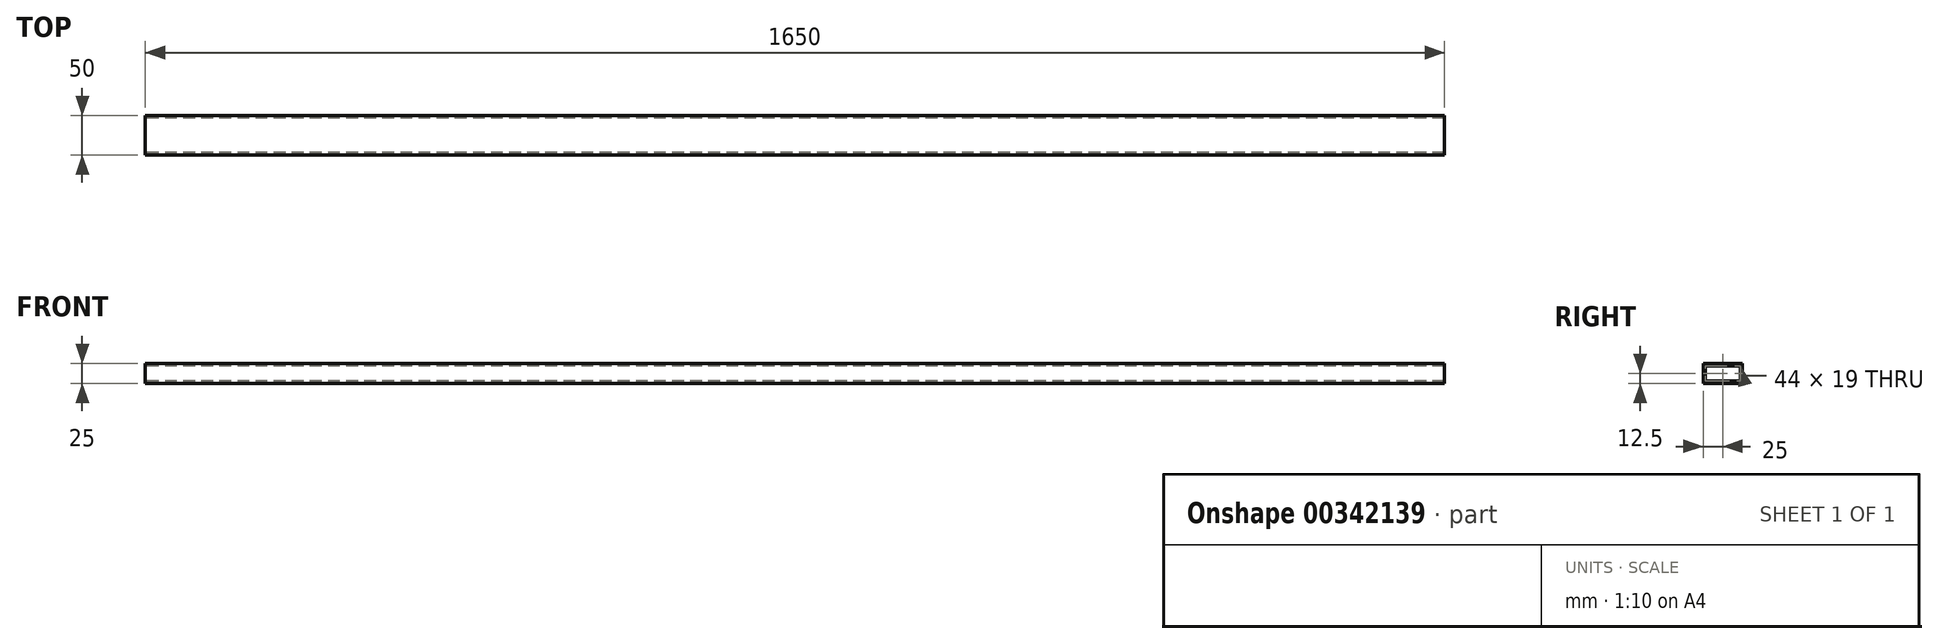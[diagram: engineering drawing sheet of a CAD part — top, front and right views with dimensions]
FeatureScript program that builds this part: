
annotation { "Feature Type Name" : "Feature", "Feature Type Description" : "" }
export const myFeature = defineFeature(function(context is Context, id is Id, definition is map)
    precondition{}
    {
        {
            var Q0;
            Q0=qCreatedBy(makeId("Right.planeOp"),FACE);
            var sketch = newSketch(context, id + "F0", { "sketchPlane" : qUnion([Q0])});
            skLineSegment(sketch, "E0.bottom", {"start": v(-25, 12.5) * mm, "end": v(25, 12.5) * mm});
            skLineSegment(sketch, "E0.top", {"start": v(-25, -12.5) * mm, "end": v(25, -12.5) * mm});
            skLineSegment(sketch, "E0.left", {"start": v(-25, 12.5) * mm, "end": v(-25, -12.5) * mm});
            skLineSegment(sketch, "E0.right", {"start": v(25, 12.5) * mm, "end": v(25, -12.5) * mm});
            skPoint(sketch, "E0.middle", {"position": v(0, 0) * mm});
            skLineSegment(sketch, "E1.bottom", {"start": v(-22, 9.5) * mm, "end": v(22, 9.5) * mm});
            skLineSegment(sketch, "E1.top", {"start": v(-22, -9.5) * mm, "end": v(22, -9.5) * mm});
            skLineSegment(sketch, "E1.left", {"start": v(-22, 9.5) * mm, "end": v(-22, -9.5) * mm});
            skLineSegment(sketch, "E1.right", {"start": v(22, 9.5) * mm, "end": v(22, -9.5) * mm});
            skSolve(sketch);
        }
        {
            var Q0;
            Q0=makeQuery(id+"F0.imprint","IMPRINT",FACE,{"disambiguationData":[TD([[makeQuery(id+"F0.imprint","IMPRINT",EDGE,{"derivedFrom":sQuery(id+"F0.wireOp",EDGE,"E0.bottom")}),-1.0]])]});
            extrude(context, id + "F1", {"entities" : qUnion([Q0]), "endBound" : BoundingType.SYMMETRIC, "depth" : 1650 * mm});
        }
    });
